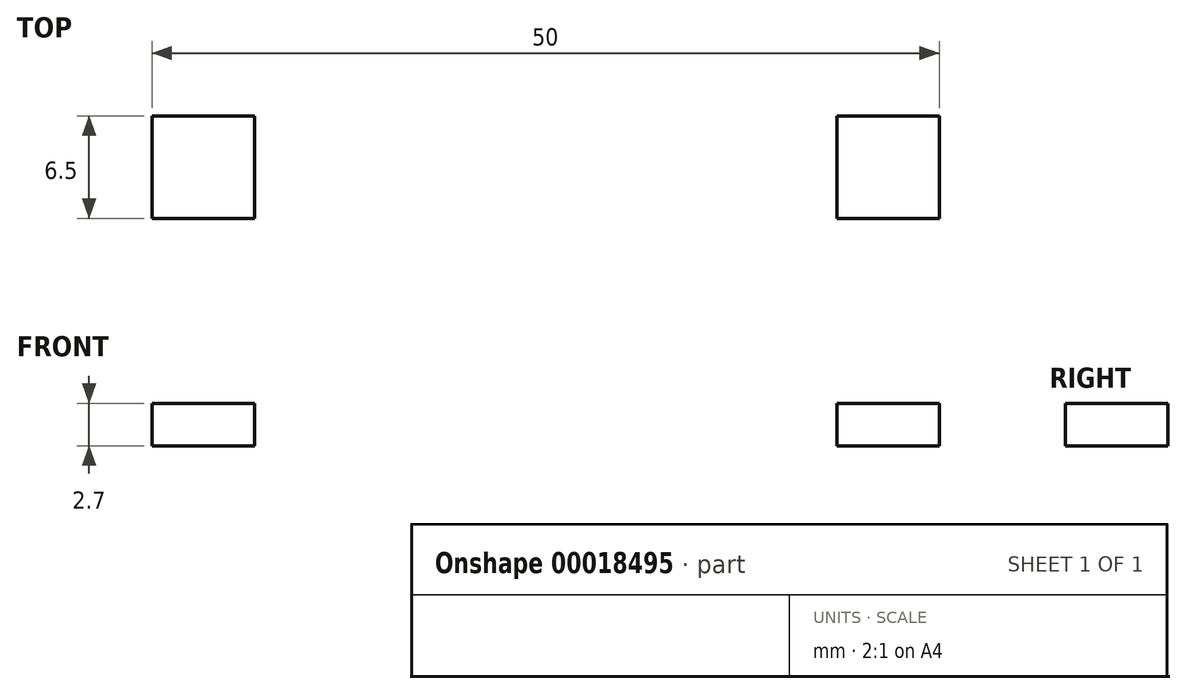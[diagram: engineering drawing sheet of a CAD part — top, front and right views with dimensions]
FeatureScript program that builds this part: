
annotation { "Feature Type Name" : "Feature", "Feature Type Description" : "" }
export const myFeature = defineFeature(function(context is Context, id is Id, definition is map)
    precondition{}
    {
        {
            var Q0;
            Q0=qCreatedBy(makeId("Top.planeOp"),FACE);
            var sketch = newSketch(context, id + "F0", { "sketchPlane" : qUnion([Q0])});
            skLineSegment(sketch, "E0.rect.bottom", {"start": v(-25, 25) * mm, "end": v(25, 25) * mm});
            skLineSegment(sketch, "E0.rect.top", {"start": v(-25, -25) * mm, "end": v(25, -25) * mm});
            skLineSegment(sketch, "E0.rect.left", {"start": v(-25, 25) * mm, "end": v(-25, -25) * mm});
            skLineSegment(sketch, "E0.rect.right", {"start": v(25, 25) * mm, "end": v(25, -25) * mm});
            skPoint(sketch, "E0.rect.middle", {"position": v(0, 0) * mm});
            skLineSegment(sketch, "E1.bottom", {"start": v(-25, 25) * mm, "end": v(-18.5, 25) * mm});
            skLineSegment(sketch, "E1.top", {"start": v(-25, 18.5) * mm, "end": v(-18.5, 18.5) * mm});
            skLineSegment(sketch, "E1.left", {"start": v(-25, 25) * mm, "end": v(-25, 18.5) * mm});
            skLineSegment(sketch, "E1.right", {"start": v(-18.5, 25) * mm, "end": v(-18.5, 18.5) * mm});
            skLineSegment(sketch, "E2.bottom", {"start": v(25, 25) * mm, "end": v(18.5, 25) * mm});
            skLineSegment(sketch, "E2.top", {"start": v(25, 18.5) * mm, "end": v(18.5, 18.5) * mm});
            skLineSegment(sketch, "E2.left", {"start": v(25, 25) * mm, "end": v(25, 18.5) * mm});
            skLineSegment(sketch, "E2.right", {"start": v(18.5, 25) * mm, "end": v(18.5, 18.5) * mm});
            skLineSegment(sketch, "E3.bottom", {"start": v(-25, -25) * mm, "end": v(-18.5, -25) * mm});
            skLineSegment(sketch, "E3.top", {"start": v(-25, -18.5) * mm, "end": v(-18.5, -18.5) * mm});
            skLineSegment(sketch, "E3.left", {"start": v(-25, -25) * mm, "end": v(-25, -18.5) * mm});
            skLineSegment(sketch, "E3.right", {"start": v(-18.5, -25) * mm, "end": v(-18.5, -18.5) * mm});
            skLineSegment(sketch, "E4.bottom", {"start": v(25, -25) * mm, "end": v(18.5, -25) * mm});
            skLineSegment(sketch, "E4.top", {"start": v(25, -18.5) * mm, "end": v(18.5, -18.5) * mm});
            skLineSegment(sketch, "E4.left", {"start": v(25, -25) * mm, "end": v(25, -18.5) * mm});
            skLineSegment(sketch, "E4.right", {"start": v(18.5, -25) * mm, "end": v(18.5, -18.5) * mm});
            skSolve(sketch);
        }
        {
            var Q0;
            Q0=makeQuery(id+"F0.imprint","IMPRINT",FACE,{"disambiguationData":[TD([[makeQuery(id+"F0.imprint","IMPRINT",EDGE,{"derivedFrom":sQuery(id+"F0.wireOp",EDGE,"E0.rect.bottom")}),-1.0]])]});
            extrude(context, id + "F1", {"entities" : qUnion([Q0]), "oppositeDirection" : true, "depth" : 2.7 * mm});
        }
        {
            var Q0;
            Q0=makeQuery(id+"F1.opExtrude","CAP_FACE",FACE,{"disambiguationData":[OSD([sQuery(id+"F0.wireOp",EDGE,"E0.rect.bottom"),sQuery(id+"F0.wireOp",EDGE,"E0.rect.top"),sQuery(id+"F0.wireOp",EDGE,"E0.rect.left"),sQuery(id+"F0.wireOp",EDGE,"E0.rect.right"),sQuery(id+"F0.wireOp",EDGE,"E1.top"),sQuery(id+"F0.wireOp",EDGE,"E1.right"),sQuery(id+"F0.wireOp",EDGE,"E2.top"),sQuery(id+"F0.wireOp",EDGE,"E2.right"),sQuery(id+"F0.wireOp",EDGE,"E3.top"),sQuery(id+"F0.wireOp",EDGE,"E3.right"),sQuery(id+"F0.wireOp",EDGE,"E4.top"),sQuery(id+"F0.wireOp",EDGE,"E4.right")])],"isStart":true});
            var sketch = newSketch(context, id + "F2", { "sketchPlane" : qUnion([Q0])});
            skCircle(sketch, "E5", {"center": v(0, 0) * mm, "radius": 7.5 * mm});
            skSolve(sketch);
        }
        {
            var Q0;
            Q0=makeQuery(id+"F2.imprint","IMPRINT",FACE,{"disambiguationData":[TD([[makeQuery(id+"F2.imprint","IMPRINT",EDGE,{"derivedFrom":sQuery(id+"F2.wireOp",EDGE,"E5")}),1.0]])]});
            extrude(context, id + "F3", {"entities" : qUnion([Q0]), "operationType" : NewBodyOperationType.REMOVE, "oppositeDirection" : true, "depth" : 2.7 * mm});
        }
    });
